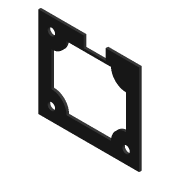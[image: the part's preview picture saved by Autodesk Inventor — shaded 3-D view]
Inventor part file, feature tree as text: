
AUTODESK INVENTOR PART (.ipt)
format: ipt  version: 2015 SP1 (Build 190203100, 203)  size: 153,088 bytes
history: native  units: mm
features: extrude x2, other x1, sketch x1
ambient origin geometry x8: Origin, YZ Plane, XZ Plane, XY Plane, X Axis, Y Axis, Z Axis, Center Point
bodies: Body1 (feature_tree)
feature tree (4):
  other  "Твердое тело1"
  sketch  "Эскиз1"
  extrude  "Выдавливание1"  Depth=1.0mm TaperAngle=0.0deg
  extrude  "Выдавливание2"  Depth=10.0mm TaperAngle=0.0deg
